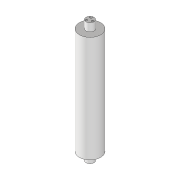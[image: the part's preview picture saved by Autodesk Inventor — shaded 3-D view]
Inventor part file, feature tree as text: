
AUTODESK INVENTOR PART (.ipt)
format: ipt  version: 2020 (Build 240168000, 168)  size: 101,376 bytes
history: native  units: mm
features: sketch x3, extrude x2, hole x1, mirror x1
ambient origin geometry x8: Origin, YZ Plane, XZ Plane, XY Plane, X Axis, Y Axis, Z Axis, Center Point
bodies: Volumenkörper1 (feature_tree)
feature tree (7):
  extrude  "Extrusion1"  Depth=200.0mm TaperAngle=0.0deg
  extrude  "Extrusion2"  Depth=30.0mm TaperAngle=0.0deg
  hole  "Bohrung1"  [1 undecoded]
  mirror  "Spiegeln1"
  sketch  "Skizze1"  dims[d0=80.0mm d1=200.0mm d2=0.0mm]
  sketch  "Skizze2"  dims[d3=30.0mm d4=30.0mm d5=0.0mm]
  sketch  "Skizze3"  dims[d6=120.0deg d7=120.0deg d8=20.0mm d9=8.0mm d10=6.0mm d11=4.0mm d12=2.0mm d13=90.0deg d14=2.0mm d15=20.594885mm]
note: 1 required parameter value undecoded (feature->parameter linkage not recoverable at this tier; creation-order binding heuristic only, values carry confidence <= 0.55)
